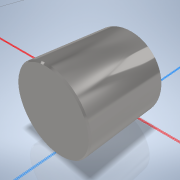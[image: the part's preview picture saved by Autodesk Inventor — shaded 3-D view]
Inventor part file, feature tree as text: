
AUTODESK INVENTOR PART (.ipt)
format: ipt  version: 2021 (Build 250183000, 183)  size: 114,176 bytes
history: native  units: mm
features: other x4, reference x2, extrude x1, chamfer x1, sketch x1
ambient origin geometry x8: Origin, YZ Plane, XZ Plane, XY Plane, X Axis, Y Axis, Z Axis, Center Point
bodies: Body1 (feature_tree)
feature tree (9):
  other  "Bryła1"
  extrude  "Wyciągnięcie proste1"  Depth=20.0mm
  chamfer  "Faza1"  Distance=20.0mm
  sketch  "Szkic1"
  reference  "Odniesienie1"
  reference  "Odniesienie2"
  parser-record x1  (decoder bookkeeping rows leaked as tree rows — omitted from the tree; the rows remain in map.json)
  other  "model tensometru.iam"
  other  "szklo:1"
note: 1 file-system path scrubbed to <path> (originals preserved in map.json)
